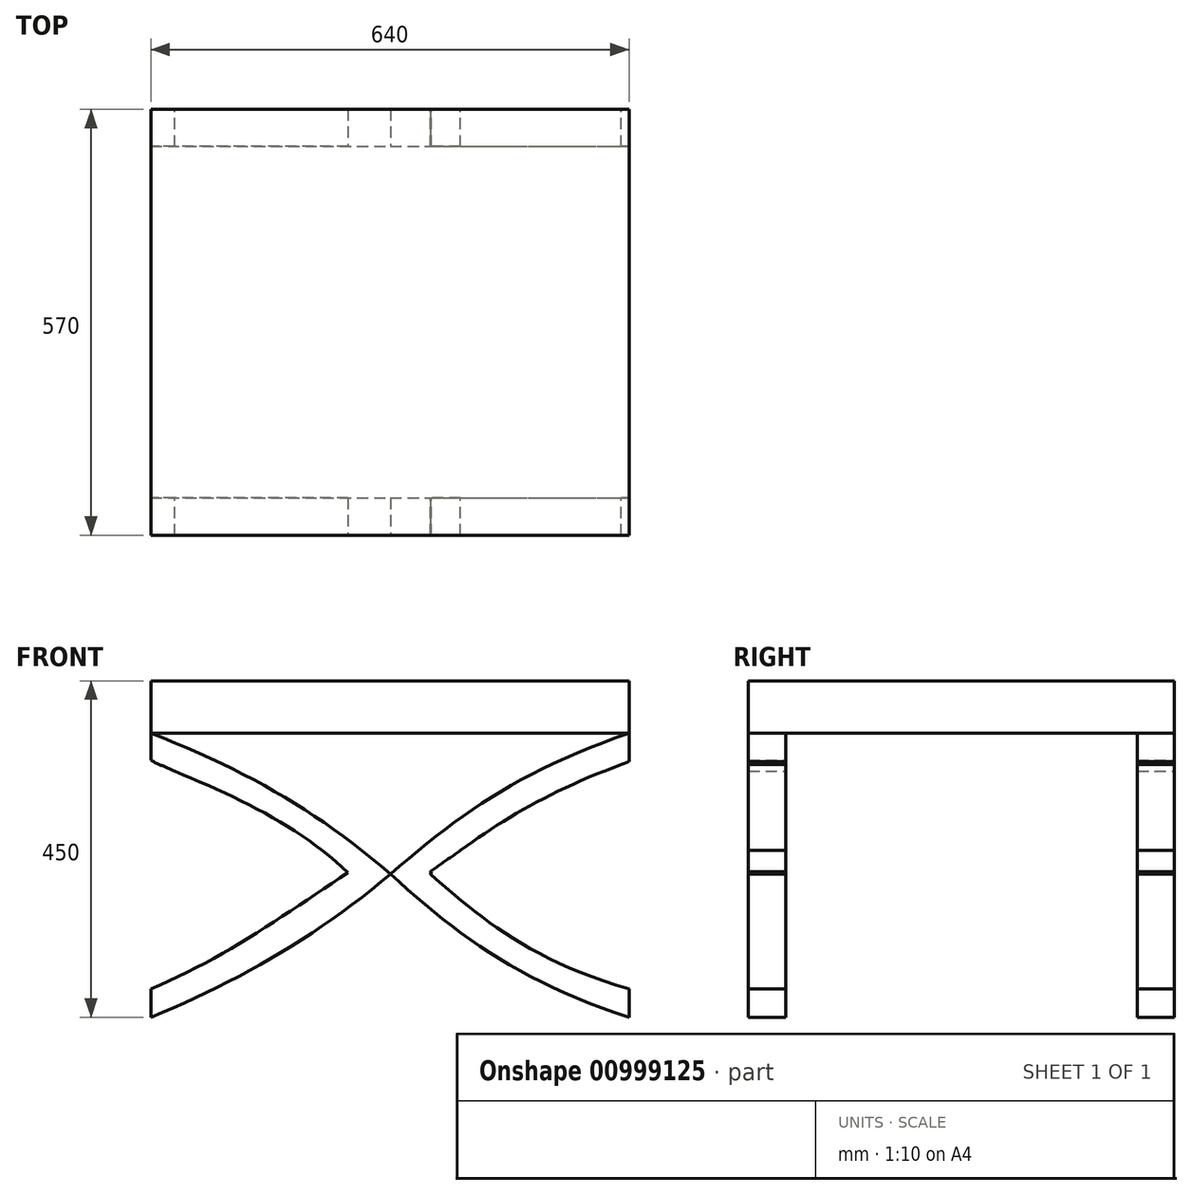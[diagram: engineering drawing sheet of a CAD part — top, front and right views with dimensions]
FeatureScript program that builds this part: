
annotation { "Feature Type Name" : "Feature", "Feature Type Description" : "" }
export const myFeature = defineFeature(function(context is Context, id is Id, definition is map)
    precondition{}
    {
        {
            var Q0;
            Q0=qCreatedBy(makeId("Top.planeOp"),FACE);
            var sketch = newSketch(context, id + "F0", { "sketchPlane" : qUnion([Q0])});
            skLineSegment(sketch, "E0.bottom", {"start": v(320, 285) * mm, "end": v(-320, 285) * mm});
            skLineSegment(sketch, "E0.top", {"start": v(320, -285) * mm, "end": v(-320, -285) * mm});
            skLineSegment(sketch, "E0.left", {"start": v(320, 285) * mm, "end": v(320, -285) * mm});
            skLineSegment(sketch, "E0.right", {"start": v(-320, 285) * mm, "end": v(-320, -285) * mm});
            skPoint(sketch, "E0.middle", {"position": v(0, 0) * mm});
            skSolve(sketch);
        }
        {
            var Q0;
            Q0 = qSketchRegion(id + "F0", true);
            extrude(context, id + "F1", {"entities" : qUnion([Q0]), "depth" : 450 * mm, "offsetDistance" : 25 * mm});
        }
        {
            var Q0;
            Q0=makeQuery(id+"F1.opExtrude","SWEPT_FACE",FACE,{"disambiguationData":[OSD([sQuery(id+"F0.wireOp",EDGE,"E0.top")])]});
            var sketch = newSketch(context, id + "F2", { "sketchPlane" : qUnion([Q0])});
            skLineSegment(sketch, "E1", {"start": v(320, 380) * mm, "end": v(-320, 380) * mm});
            skFitSpline(sketch, "E2", {"points": [v(-320, 380) * mm, v(0.83, 191.67) * mm], "startDerivative": vector(386.13, -149.74) * mm, "endDerivative": vector(289.74, -249.63) * mm});
            skFitSpline(sketch, "E3", {"points": [v(0.83, 191.67) * mm, v(320, 380) * mm], "startDerivative": vector(287.8, 249.63) * mm, "endDerivative": vector(432.8, 149.74) * mm});
            skFitSpline(sketch, "E4", {"points": [v(-320, 0) * mm, v(0.83, 191.67) * mm], "startDerivative": vector(344.7, 139.3) * mm, "endDerivative": vector(288.67, 245.7) * mm});
            skFitSpline(sketch, "E5", {"points": [v(0.83, 191.67) * mm, v(320, 0) * mm], "startDerivative": vector(266.92, -245.7) * mm, "endDerivative": vector(432.8, -139.3) * mm});
            skFitSpline(sketch, "E6", {"points": [v(-56.02, 193.63) * mm, v(-320, 341.67) * mm], "startDerivative": vector(-208.2, 199.28) * mm, "endDerivative": vector(-298.2, 116) * mm});
            skFitSpline(sketch, "E7", {"points": [v(-56.02, 193.63) * mm, v(-320, 37.97) * mm], "startDerivative": vector(-249.85, -166.56) * mm, "endDerivative": vector(-283.33, -116) * mm});
            skFitSpline(sketch, "E8", {"points": [v(54.03, 191.67) * mm, v(320, 341.67) * mm], "startDerivative": vector(220.1, 178.4) * mm, "endDerivative": vector(339.84, 118.97) * mm});
            skFitSpline(sketch, "E9", {"points": [v(54.03, 191.67) * mm, v(320, 37.97) * mm], "startDerivative": vector(184.41, -160.68) * mm, "endDerivative": vector(408.25, -116) * mm});
            skSolve(sketch);
        }
        {
            var Q0;
            Q0=makeQuery(id+"F2.imprint","IMPRINT",FACE,{"disambiguationData":[TD([[makeQuery(id+"F2.imprint","IMPRINT",EDGE,{"derivedFrom":sQuery(id+"F2.wireOp",EDGE,"E1")}),1.0]])]});
            extrude(context, id + "F3", {"entities" : qUnion([Q0]), "operationType" : NewBodyOperationType.REMOVE, "endBound" : BoundingType.THROUGH_ALL, "oppositeDirection" : true, "depth" : 25 * mm, "offsetDistance" : 25 * mm});
        }
        {
            var Q0;
            Q0=makeQuery(id+"F2.imprint","IMPRINT",FACE,{"disambiguationData":[TD([[makeQuery(id+"F2.imprint","IMPRINT",EDGE,{"derivedFrom":sQuery(id+"F2.wireOp",EDGE,"E4")}),-1.0]])]});
            extrude(context, id + "F4", {"entities" : qUnion([Q0]), "operationType" : NewBodyOperationType.REMOVE, "endBound" : BoundingType.THROUGH_ALL, "oppositeDirection" : true, "depth" : 25 * mm, "offsetDistance" : 25 * mm});
        }
        {
            var Q0;
            {var subQ1=sQuery(id+"F0.wireOp",EDGE,"E0.left");Q0=makeQuery(id+"F3.boolean.opBoolean","SPLIT",FACE,{"disambiguationData":[TD([makeQuery(id+"F3.opExtrude","SWEPT_FACE",FACE,{"disambiguationData":[OSD([sQuery(id+"F2.wireOp",EDGE,"E3")])]})])],"derivedFrom":makeQuery(id+"F1.opExtrude","SWEPT_FACE",FACE,{"disambiguationData":[OSD([subQ1])]})});}
            var sketch = newSketch(context, id + "F5", { "sketchPlane" : qUnion([Q0])});
            skLineSegment(sketch, "E10.bottom", {"start": v(-235, 0) * mm, "end": v(235, 0) * mm});
            skLineSegment(sketch, "E10.top", {"start": v(-235, 380) * mm, "end": v(235, 380) * mm});
            skLineSegment(sketch, "E10.left", {"start": v(-235, 0) * mm, "end": v(-235, 380) * mm});
            skLineSegment(sketch, "E10.right", {"start": v(235, 0) * mm, "end": v(235, 380) * mm});
            skSolve(sketch);
        }
        {
            var Q0;
            Q0=makeQuery(id+"F5.imprint","IMPRINT",FACE,{"disambiguationData":[TD([[makeQuery(id+"F5.imprint","IMPRINT",EDGE,{"derivedFrom":sQuery(id+"F5.wireOp",EDGE,"E10.bottom")}),-1.0]])]});
            extrude(context, id + "F6", {"entities" : qUnion([Q0]), "operationType" : NewBodyOperationType.REMOVE, "endBound" : BoundingType.THROUGH_ALL, "oppositeDirection" : true, "depth" : 25 * mm, "offsetDistance" : 25 * mm});
        }
        {
            var Q0;
            {var subQ1=sQuery(id+"F0.wireOp",EDGE,"E0.right");Q0=makeQuery(id+"F3.boolean.opBoolean","SPLIT",FACE,{"disambiguationData":[TD([makeQuery(id+"F3.opExtrude","SWEPT_FACE",FACE,{"disambiguationData":[OSD([sQuery(id+"F2.wireOp",EDGE,"E2")])]})])],"derivedFrom":makeQuery(id+"F1.opExtrude","SWEPT_FACE",FACE,{"disambiguationData":[OSD([subQ1])]})});}
            var sketch = newSketch(context, id + "F7", { "sketchPlane" : qUnion([Q0])});
            skLineSegment(sketch, "E11.bottom", {"start": v(-235.47, 0) * mm, "end": v(234.48, 0) * mm});
            skLineSegment(sketch, "E11.top", {"start": v(-235.47, 380) * mm, "end": v(234.48, 380) * mm});
            skLineSegment(sketch, "E11.left", {"start": v(-235.47, 0) * mm, "end": v(-235.47, 380) * mm});
            skLineSegment(sketch, "E11.right", {"start": v(234.48, 0) * mm, "end": v(234.48, 380) * mm});
            skSolve(sketch);
        }
        {
            var Q0;
            Q0=makeQuery(id+"F7.imprint","IMPRINT",FACE,{"disambiguationData":[TD([[makeQuery(id+"F7.imprint","IMPRINT",EDGE,{"derivedFrom":sQuery(id+"F7.wireOp",EDGE,"E11.bottom")}),1.0]])]});
            extrude(context, id + "F8", {"entities" : qUnion([Q0]), "operationType" : NewBodyOperationType.REMOVE, "endBound" : BoundingType.THROUGH_ALL, "oppositeDirection" : true, "depth" : 25 * mm, "offsetDistance" : 25 * mm});
        }
        {
            var Q0;
            {var subQ0=sQuery(id+"F2.wireOp",EDGE,"E6");Q0=makeQuery(id+"F2.imprint","IMPRINT",FACE,{"disambiguationData":[TD([[makeQuery(id+"F2.imprint","IMPRINT",EDGE,{"derivedFrom":subQ0}),1.0]])]});}
            extrude(context, id + "F9", {"entities" : qUnion([Q0]), "operationType" : NewBodyOperationType.REMOVE, "endBound" : BoundingType.THROUGH_ALL, "oppositeDirection" : true, "depth" : 25 * mm, "offsetDistance" : 25 * mm});
        }
        {
            var Q0;
            {var subQ0=sQuery(id+"F2.wireOp",EDGE,"E8");Q0=makeQuery(id+"F2.imprint","IMPRINT",FACE,{"disambiguationData":[TD([[makeQuery(id+"F2.imprint","IMPRINT",EDGE,{"derivedFrom":subQ0}),-1.0]])]});}
            var Q1;
            {var subQ0=sQuery(id+"F2.wireOp",EDGE,"E6");Q1=makeQuery(id+"F2.imprint","IMPRINT",FACE,{"disambiguationData":[TD([[makeQuery(id+"F2.imprint","IMPRINT",EDGE,{"derivedFrom":subQ0}),1.0]])]});}
            extrude(context, id + "F10", {"entities" : qUnion([Q0, Q1]), "operationType" : NewBodyOperationType.REMOVE, "endBound" : BoundingType.THROUGH_ALL, "oppositeDirection" : true, "depth" : 25 * mm, "offsetDistance" : 25 * mm});
        }
        {
            var Q0;
            {var subQ0=sQuery(id+"F0.wireOp",EDGE,"E0.left");var subQ1=makeQuery(id+"F1.opExtrude","SWEPT_FACE",FACE,{"disambiguationData":[OSD([subQ0])]});var subQ4=sQuery(id+"F0.wireOp",EDGE,"E0.bottom");Q0=makeQuery(id+"F4.boolean.opBoolean","SPLIT",FACE,{"disambiguationData":[TD([subQ1])],"derivedFrom":makeQuery(id+"F3.boolean.opBoolean","SPLIT",FACE,{"disambiguationData":[TD([makeQuery(id+"F3.opExtrude","SWEPT_FACE",FACE,{"disambiguationData":[OSD([sQuery(id+"F2.wireOp",EDGE,"E2")])]})])],"derivedFrom":makeQuery(id+"F1.opExtrude","SWEPT_FACE",FACE,{"disambiguationData":[OSD([subQ4])]})})});}
            var sketch = newSketch(context, id + "F11", { "sketchPlane" : qUnion([Q0])});
            skFitSpline(sketch, "E12", {"points": [v(-320, 342.02) * mm, v(-54.04, 194.64) * mm], "startDerivative": vector(296.58, -114.16) * mm, "endDerivative": vector(251.46, -182.24) * mm});
            skFitSpline(sketch, "E13", {"points": [v(-54.04, 194.64) * mm, v(-320, 39.25) * mm], "startDerivative": vector(-215.77, -198.48) * mm, "endDerivative": vector(-323.35, -62.46) * mm});
            skSolve(sketch);
        }
        {
            var Q0;
            {var subQ0=sQuery(id+"F11.wireOp",EDGE,"E12");Q0=makeQuery(id+"F11.imprint","IMPRINT",FACE,{"disambiguationData":[TD([[makeQuery(id+"F11.imprint","IMPRINT",EDGE,{"derivedFrom":subQ0}),-1.0]])]});}
            extrude(context, id + "F12", {"entities" : qUnion([Q0]), "operationType" : NewBodyOperationType.REMOVE, "endBound" : BoundingType.THROUGH_ALL, "oppositeDirection" : true, "depth" : 25 * mm, "offsetDistance" : 25 * mm});
        }
        {
            var Q0;
            {var subQ0=sQuery(id+"F0.wireOp",EDGE,"E0.right");var subQ1=makeQuery(id+"F1.opExtrude","SWEPT_FACE",FACE,{"disambiguationData":[OSD([subQ0])]});var subQ2=makeQuery(id+"F3.opExtrude","SWEPT_FACE",FACE,{"disambiguationData":[OSD([sQuery(id+"F2.wireOp",EDGE,"E2")])]});var subQ4=sQuery(id+"F0.wireOp",EDGE,"E0.bottom");Q0=makeQuery(id+"F4.boolean.opBoolean","SPLIT",FACE,{"disambiguationData":[TD([subQ1])],"derivedFrom":makeQuery(id+"F3.boolean.opBoolean","SPLIT",FACE,{"disambiguationData":[TD([subQ2])],"derivedFrom":makeQuery(id+"F1.opExtrude","SWEPT_FACE",FACE,{"disambiguationData":[OSD([subQ4])]})})});}
            var sketch = newSketch(context, id + "F13", { "sketchPlane" : qUnion([Q0])});
            skFitSpline(sketch, "E14", {"points": [v(58.45, 194.91) * mm, v(320, 343.63) * mm], "startDerivative": vector(237.95, 226.05) * mm, "endDerivative": vector(258.19, 121.95) * mm});
            skFitSpline(sketch, "E15", {"points": [v(58.45, 194.91) * mm, v(320, 38.26) * mm], "startDerivative": vector(249.85, -190.36) * mm, "endDerivative": vector(270.08, -130.87) * mm});
            skSolve(sketch);
        }
        {
            var Q0;
            {var subQ0=sQuery(id+"F13.wireOp",EDGE,"E14");Q0=makeQuery(id+"F13.imprint","IMPRINT",FACE,{"disambiguationData":[TD([[makeQuery(id+"F13.imprint","IMPRINT",EDGE,{"derivedFrom":subQ0}),-1.0]])]});}
            extrude(context, id + "F14", {"entities" : qUnion([Q0]), "operationType" : NewBodyOperationType.REMOVE, "endBound" : BoundingType.THROUGH_ALL, "oppositeDirection" : true, "depth" : 25 * mm, "offsetDistance" : 25 * mm});
        }
    });
